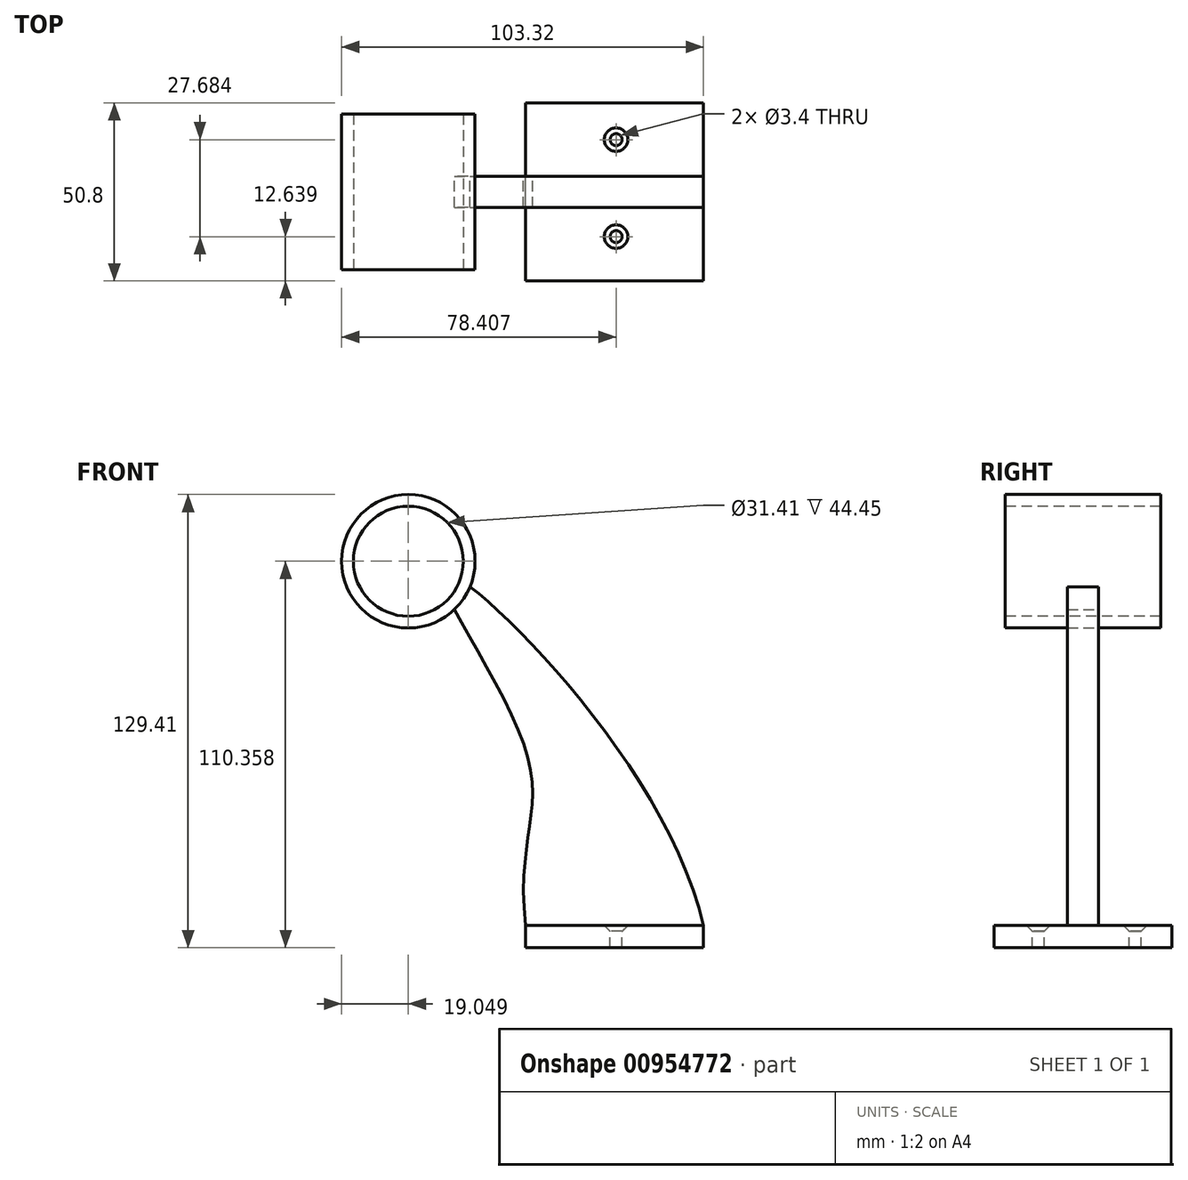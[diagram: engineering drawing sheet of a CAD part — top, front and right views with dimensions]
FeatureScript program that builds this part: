
annotation { "Feature Type Name" : "Feature", "Feature Type Description" : "" }
export const myFeature = defineFeature(function(context is Context, id is Id, definition is map)
    precondition{}
    {
        {
            var Q0;
            Q0=qCreatedBy(makeId("Front.planeOp"),FACE);
            var sketch = newSketch(context, id + "F0", { "sketchPlane" : qUnion([Q0])});
            skLineSegment(sketch, "E0.bottom", {"start": v(65.82, -40.08) * mm, "end": v(15.02, -40.08) * mm});
            skLineSegment(sketch, "E0.top", {"start": v(65.82, -33.73) * mm, "end": v(15.02, -33.73) * mm});
            skLineSegment(sketch, "E0.left", {"start": v(65.82, -40.08) * mm, "end": v(65.82, -33.73) * mm});
            skLineSegment(sketch, "E0.right", {"start": v(15.02, -40.08) * mm, "end": v(15.02, -33.73) * mm});
            skPoint(sketch, "E0.middle", {"position": v(40.42, -36.9) * mm});
            skFitSpline(sketch, "E1", {"points": [v(15.02, -33.73) * mm, v(15.02, 16.52) * mm, v(-9.41, 67.4) * mm, v(65.82, -33.73) * mm], "startDerivative": vector(-30, 268.28) * mm, "endDerivative": vector(75.37, -336.6) * mm});
            skSolve(sketch);
        }
        {
            var Q0;
            Q0=makeQuery(id+"F0.imprint","IMPRINT",FACE,{"disambiguationData":[TD([[makeQuery(id+"F0.imprint","IMPRINT",EDGE,{"derivedFrom":sQuery(id+"F0.wireOp",EDGE,"E0.bottom")}),-1.0]])]});
            extrude(context, id + "F1", {"entities" : qUnion([Q0]), "endBound" : BoundingType.SYMMETRIC, "depth" : 50.8 * mm, "offsetDistance" : 25.4 * mm});
        }
        {
            var Q0;
            Q0 = qSketchRegion(id + "F0", true);
            extrude(context, id + "F2", {"entities" : qUnion([Q0]), "operationType" : NewBodyOperationType.ADD, "endBound" : BoundingType.SYMMETRIC, "depth" : 8.9 * mm, "offsetDistance" : 25.4 * mm});
        }
        {
            var Q0;
            Q0=qCreatedBy(makeId("Front.planeOp"),FACE);
            var sketch = newSketch(context, id + "F3", { "sketchPlane" : qUnion([Q0])});
            skCircle(sketch, "E2", {"center": v(-18.45, 70.28) * mm, "radius": 19.05 * mm});
            skSolve(sketch);
        }
        {
            var Q0;
            Q0=makeQuery(id+"F3.imprint","IMPRINT",FACE,{"disambiguationData":[TD([[makeQuery(id+"F3.imprint","IMPRINT",EDGE,{"derivedFrom":sQuery(id+"F3.wireOp",EDGE,"E2")}),1.0]])]});
            extrude(context, id + "F4", {"entities" : qUnion([Q0]), "operationType" : NewBodyOperationType.ADD, "endBound" : BoundingType.SYMMETRIC, "depth" : 44.45 * mm, "offsetDistance" : 25.4 * mm});
        }
        {
            var Q0;
            Q0=makeQuery(id+"F4.opExtrude","CAP_FACE",FACE,{"disambiguationData":[OSD([sQuery(id+"F3.wireOp",EDGE,"E2")])],"isStart":false});
            var sketch = newSketch(context, id + "F5", { "sketchPlane" : qUnion([Q0])});
            skCircle(sketch, "E3", {"center": v(-18.45, 70.28) * mm, "radius": 15.7 * mm});
            skSolve(sketch);
        }
        {
            var Q0;
            Q0=makeQuery(id+"F5.imprint","IMPRINT",FACE,{"disambiguationData":[TD([[makeQuery(id+"F5.imprint","IMPRINT",EDGE,{"derivedFrom":sQuery(id+"F5.wireOp",EDGE,"E3")}),1.0]])]});
            extrude(context, id + "F6", {"entities" : qUnion([Q0]), "operationType" : NewBodyOperationType.REMOVE, "oppositeDirection" : true, "depth" : 44.45 * mm, "offsetDistance" : 25.4 * mm});
        }
        {
            var Q0;
            {var subQ1=sQuery(id+"F0.wireOp",EDGE,"E0.right");var subQ2=sQuery(id+"F0.wireOp",EDGE,"E0.left");var subQ3=sQuery(id+"F0.wireOp",EDGE,"E0.bottom");var subQ4=sQuery(id+"F0.wireOp",EDGE,"E0.top");Q0=makeQuery(id+"F2.boolean.opBoolean","SPLIT",FACE,{"disambiguationData":[TD([makeQuery(id+"F1.opExtrude","CAP_FACE",FACE,{"disambiguationData":[OSD([subQ3,subQ4,subQ2,subQ1])],"isStart":true})])],"derivedFrom":makeQuery(id+"F1.opExtrude","SWEPT_FACE",FACE,{"disambiguationData":[OSD([subQ4])]})});}
            var sketch = newSketch(context, id + "F7", { "sketchPlane" : qUnion([Q0])});
            skPoint(sketch, "E4", {"position": v(40.9, 14.92) * mm});
            skPoint(sketch, "E4.positionSnap0", {"position": v(15.02, 14.92) * mm});
            skPoint(sketch, "E5", {"position": v(40.9, -12.76) * mm});
            skSolve(sketch);
        }
        {
            var Q0;
            Q0=sQuery(id+"F7.wireOp",VERTEX,"E4");
            var Q1;
            Q1=makeQuery(id+"F1.opExtrude","SWEPT_BODY",BODY,{"disambiguationData":[OSD([sQuery(id+"F0.wireOp",EDGE,"E0.bottom"),sQuery(id+"F0.wireOp",EDGE,"E0.top"),sQuery(id+"F0.wireOp",EDGE,"E0.left"),sQuery(id+"F0.wireOp",EDGE,"E0.right")])]});
            hole(context, id + "F8", {"style" : HoleStyle.C_SINK, "endStyle" : HoleEndStyle.THROUGH, "standardTappedOrClearance" : lookupTablePath({ "fit" : "Normal", "standard" : "ISO", "size" : "M3", "type" : "Clearance" }), "standardBlindInLast" : lookupTablePath({ "fit" : "Normal", "standard" : "ISO", "engagement" : "75%", "pitch" : "0.5 mm", "size" : "M3", "type" : "Clearance & tapped" }), "holeDiameter" : 3.4 * mm, "cSinkDiameter" : 6.72 * mm, "cSinkAngle" : 90 * degree, "majorDiameter" : 6.35 * mm, "isTappedThrough" : true, "tappedDepth" : 12.7 * mm, "tapClearance" : 3, "locations" : qUnion([Q0]), "scope" : qUnion([Q1])});
        }
        {
            var Q0;
            Q0=sQuery(id+"F7.wireOp",VERTEX,"E5");
            var Q1;
            Q1=makeQuery(id+"F1.opExtrude","SWEPT_BODY",BODY,{"disambiguationData":[OSD([sQuery(id+"F0.wireOp",EDGE,"E0.bottom"),sQuery(id+"F0.wireOp",EDGE,"E0.top"),sQuery(id+"F0.wireOp",EDGE,"E0.left"),sQuery(id+"F0.wireOp",EDGE,"E0.right")])]});
            hole(context, id + "F9", {"style" : HoleStyle.C_SINK, "endStyle" : HoleEndStyle.THROUGH, "standardTappedOrClearance" : lookupTablePath({ "fit" : "Normal", "standard" : "ISO", "size" : "M3", "type" : "Clearance" }), "standardBlindInLast" : lookupTablePath({ "fit" : "Normal", "standard" : "ISO", "engagement" : "75%", "pitch" : "0.5 mm", "size" : "M3", "type" : "Clearance & tapped" }), "holeDiameter" : 3.4 * mm, "cSinkDiameter" : 6.72 * mm, "cSinkAngle" : 90 * degree, "majorDiameter" : 6.35 * mm, "isTappedThrough" : true, "tappedDepth" : 12.7 * mm, "tapClearance" : 3, "locations" : qUnion([Q0]), "scope" : qUnion([Q1])});
        }
    });
